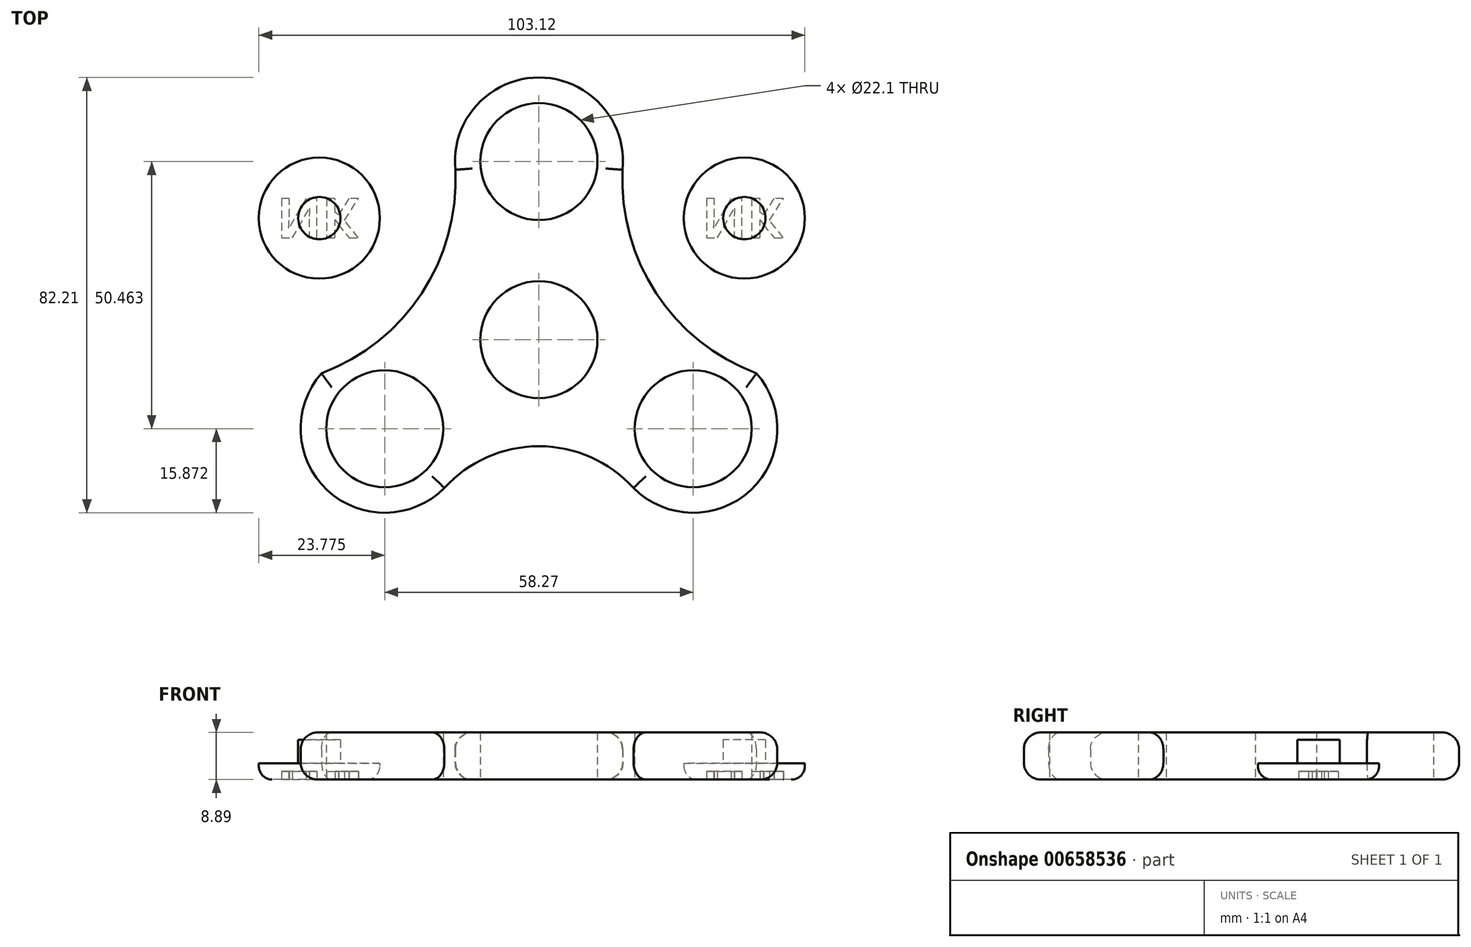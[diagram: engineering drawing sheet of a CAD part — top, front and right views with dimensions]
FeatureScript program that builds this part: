
annotation { "Feature Type Name" : "Feature", "Feature Type Description" : "" }
export const myFeature = defineFeature(function(context is Context, id is Id, definition is map)
    precondition{}
    {
        {
            var Q0;
            Q0=qCreatedBy(makeId("Top.planeOp"),FACE);
            var sketch = newSketch(context, id + "F0", { "sketchPlane" : qUnion([Q0])});
            skCircle(sketch, "E0", {"center": v(0, 61.65) * mm, "radius": 11.05 * mm});
            skCircle(sketch, "E1.1.0", {"center": v(-29.14, 11.18) * mm, "radius": 11.05 * mm});
            skCircle(sketch, "E1.2.0", {"center": v(29.14, 11.18) * mm, "radius": 11.05 * mm});
            skPoint(sketch, "E1.center", {"position": v(0, 28) * mm});
            skCircle(sketch, "E2", {"center": v(0, 28) * mm, "radius": 11.05 * mm});
            skArc(sketch, "E3", {"start": v(15.8, 60.1) * mm, "mid": v(0, 77.52) * mm, "end": v(-15.8, 60.1) * mm});
            skArc(sketch, "E4", {"start": v(17.32, 0.58) * mm, "mid": v(43.12, 3.66) * mm, "end": v(31.46, 26.89) * mm});
            skArc(sketch, "E5", {"start": v(-31.46, 26.89) * mm, "mid": v(-43.12, 3.66) * mm, "end": v(-17.32, 0.58) * mm});
            skArc(sketch, "E6", {"start": v(-41.06, 21.66) * mm, "mid": v(-22.15, 36.75) * mm, "end": v(-15.8, 60.1) * mm});
            skArc(sketch, "E7.MirrorCS", {"start": v(41.06, 21.66) * mm, "mid": v(22.15, 36.75) * mm, "end": v(15.8, 60.1) * mm});
            skArc(sketch, "E8", {"start": v(17.87, 0) * mm, "mid": v(0, 7.88) * mm, "end": v(-17.87, 0) * mm});
            skSolve(sketch);
        }
        {
            var Q0;
            Q0=makeQuery(id+"F0.imprint","IMPRINT",FACE,{"disambiguationData":[TD([[makeQuery(id+"F0.imprint","IMPRINT",EDGE,{"derivedFrom":sQuery(id+"F0.wireOp",EDGE,"E0")}),-1.0]])]});
            extrude(context, id + "F1", {"entities" : qUnion([Q0]), "depth" : 8.9 * mm, "offsetDistance" : 25.4 * mm});
        }
        {
            var Q0;
            Q0=makeQuery(id+"F1.opExtrude","CAP_EDGE",EDGE,{"disambiguationData":[OSD([sQuery(id+"F0.wireOp",EDGE,"E4")])],"isStart":false});
            var Q1;
            Q1=makeQuery(id+"F1.opExtrude","CAP_EDGE",EDGE,{"disambiguationData":[OSD([sQuery(id+"F0.wireOp",EDGE,"E7.MirrorCS")])],"isStart":false});
            var Q2;
            Q2=makeQuery(id+"F1.opExtrude","CAP_EDGE",EDGE,{"disambiguationData":[OSD([sQuery(id+"F0.wireOp",EDGE,"E3")])],"isStart":false});
            var Q3;
            Q3=makeQuery(id+"F1.opExtrude","CAP_EDGE",EDGE,{"disambiguationData":[OSD([sQuery(id+"F0.wireOp",EDGE,"E6")])],"isStart":false});
            var Q4;
            Q4=makeQuery(id+"F1.opExtrude","CAP_EDGE",EDGE,{"disambiguationData":[OSD([sQuery(id+"F0.wireOp",EDGE,"E5")])],"isStart":false});
            var Q5;
            Q5=makeQuery(id+"F1.opExtrude","CAP_EDGE",EDGE,{"disambiguationData":[OSD([sQuery(id+"F0.wireOp",EDGE,"E8")])],"isStart":false});
            var Q6;
            Q6=makeQuery(id+"F1.opExtrude","CAP_EDGE",EDGE,{"disambiguationData":[OSD([sQuery(id+"F0.wireOp",EDGE,"E5")])],"isStart":true});
            var Q7;
            Q7=makeQuery(id+"F1.opExtrude","CAP_EDGE",EDGE,{"disambiguationData":[OSD([sQuery(id+"F0.wireOp",EDGE,"E8")])],"isStart":true});
            var Q8;
            Q8=makeQuery(id+"F1.opExtrude","CAP_EDGE",EDGE,{"disambiguationData":[OSD([sQuery(id+"F0.wireOp",EDGE,"E4")])],"isStart":true});
            var Q9;
            Q9=makeQuery(id+"F1.opExtrude","CAP_EDGE",EDGE,{"disambiguationData":[OSD([sQuery(id+"F0.wireOp",EDGE,"E7.MirrorCS")])],"isStart":true});
            var Q10;
            Q10=makeQuery(id+"F1.opExtrude","CAP_EDGE",EDGE,{"disambiguationData":[OSD([sQuery(id+"F0.wireOp",EDGE,"E3")])],"isStart":true});
            var Q11;
            Q11=makeQuery(id+"F1.opExtrude","CAP_EDGE",EDGE,{"disambiguationData":[OSD([sQuery(id+"F0.wireOp",EDGE,"E6")])],"isStart":true});
            fillet(context, id + "F2", {"entities" : qUnion([Q0, Q1, Q2, Q3, Q4, Q5, Q6, Q7, Q8, Q9, Q10, Q11]), "radius" : 3.17 * mm, "tangentPropagation" : true, "allowEdgeOverflow" : false});
        }
        {
            var Q0;
            Q0=qCreatedBy(makeId("Top.planeOp"),FACE);
            var sketch = newSketch(context, id + "F3", { "sketchPlane" : qUnion([Q0])});
            skCircle(sketch, "E9", {"center": v(38.78, 50.96) * mm, "radius": 11.43 * mm});
            skSolve(sketch);
        }
        {
            var Q0;
            Q0=makeQuery(id+"F3.imprint","IMPRINT",FACE,{"disambiguationData":[TD([[makeQuery(id+"F3.imprint","IMPRINT",EDGE,{"derivedFrom":sQuery(id+"F3.wireOp",EDGE,"E9")}),1.0]])]});
            extrude(context, id + "F4", {"entities" : qUnion([Q0]), "depth" : 3.05 * mm, "offsetDistance" : 25.4 * mm});
        }
        {
            var Q0;
            Q0=makeQuery(id+"F4.opExtrude","CAP_FACE",FACE,{"disambiguationData":[OSD([sQuery(id+"F3.wireOp",EDGE,"E9")])],"isStart":false});
            var sketch = newSketch(context, id + "F5", { "sketchPlane" : qUnion([Q0])});
            skCircle(sketch, "E10", {"center": v(38.78, 50.96) * mm, "radius": 4 * mm});
            skSolve(sketch);
        }
        {
            var Q0;
            Q0=makeQuery(id+"F5.imprint","IMPRINT",FACE,{"disambiguationData":[TD([[makeQuery(id+"F5.imprint","IMPRINT",EDGE,{"derivedFrom":sQuery(id+"F5.wireOp",EDGE,"E10")}),1.0]])]});
            extrude(context, id + "F6", {"entities" : qUnion([Q0]), "operationType" : NewBodyOperationType.ADD, "depth" : 4.44 * mm, "offsetDistance" : 25.4 * mm});
        }
        {
            var Q0;
            Q0=makeQuery(id+"F4.opExtrude","CAP_EDGE",EDGE,{"disambiguationData":[OSD([sQuery(id+"F3.wireOp",EDGE,"E9")])],"isStart":true});
            fillet(context, id + "F7", {"entities" : qUnion([Q0]), "radius" : 2.54 * mm, "tangentPropagation" : true, "allowEdgeOverflow" : false});
        }
        {
            var Q0;
            Q0=makeQuery(id+"F4.opExtrude","CAP_FACE",FACE,{"disambiguationData":[OSD([sQuery(id+"F3.wireOp",EDGE,"E9")])],"isStart":true});
            var sketch = newSketch(context, id + "F8", { "sketchPlane" : qUnion([Q0])});
            skText(sketch, "E11", { "text": "NK", "fontName": "OpenSans-Bold.ttf"});
            const initialGuessF8  = {"E11": [0.03074, -0.0547, 1, 0, 0.00752]};
            skSetInitialGuess(sketch, initialGuessF8);
            skSolve(sketch);
        }
        {
            var Q0;
            Q0 = qSketchRegion(id + "F8", true);
            extrude(context, id + "F9", {"entities" : qUnion([Q0]), "operationType" : NewBodyOperationType.REMOVE, "oppositeDirection" : true, "depth" : 1.52 * mm, "offsetDistance" : 25.4 * mm});
        }
        {
            var Q0;
            Q0=makeQuery(id+"F4.opExtrude","SWEPT_BODY",BODY,{"disambiguationData":[OSD([sQuery(id+"F3.wireOp",EDGE,"E9")])]});
            transform(context, id + "F10", {"entities" : qUnion([Q0]), "transformType" : TransformType.TRANSLATION_3D, "dx" : -80.26 * mm, "dy" : 0 * mm, "dz" : 0 * mm, "makeCopy" : true});
        }
    });
